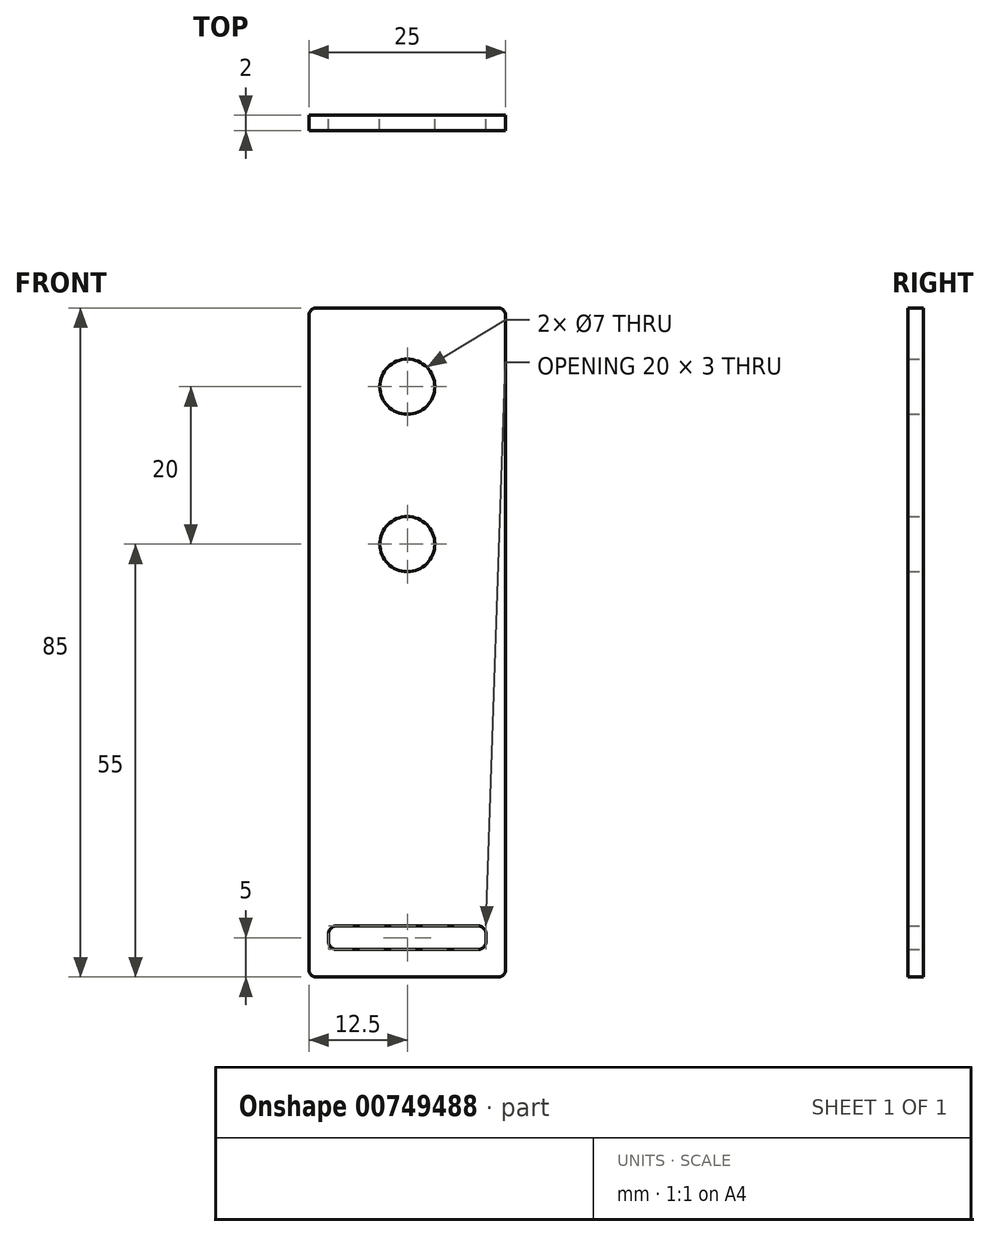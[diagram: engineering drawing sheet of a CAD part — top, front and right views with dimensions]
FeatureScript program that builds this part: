
annotation { "Feature Type Name" : "Feature", "Feature Type Description" : "" }
export const myFeature = defineFeature(function(context is Context, id is Id, definition is map)
    precondition{}
    {
        {
            var Q0;
            Q0=qCreatedBy(makeId("Front.planeOp"), FACE);
            var sketch = newSketch(context, id + "F0", { "sketchPlane" : qUnion([Q0])});
            skLineSegment(sketch, "E0.bottom", {"start": v(11.5, -42.5) * mm, "end": v(-11.5, -42.5) * mm});
            skLineSegment(sketch, "E0.top", {"start": v(11.5, 42.5) * mm, "end": v(-11.5, 42.5) * mm});
            skLineSegment(sketch, "E0.left", {"start": v(12.5, -41.5) * mm, "end": v(12.5, 41.5) * mm});
            skLineSegment(sketch, "E0.right", {"start": v(-12.5, -41.5) * mm, "end": v(-12.5, 41.5) * mm});
            skPoint(sketch, "E0.middle", {"position": v(0, 0) * mm});
            skLineSegment(sketch, "E1", {"start": v(0, 42.5) * mm, "end": v(0, -42.5) * mm, "construction": true});
            skLineSegment(sketch, "E2", {"start": v(-12.5, 32.5) * mm, "end": v(12.5, 32.5) * mm, "construction": true});
            skLineSegment(sketch, "E3", {"start": v(-12.5, 12.5) * mm, "end": v(12.5, 12.5) * mm, "construction": true});
            skLineSegment(sketch, "E4", {"start": v(-12.5, -37.5) * mm, "end": v(12.5, -37.5) * mm, "construction": true});
            skCircle(sketch, "E5", {"center": v(0, 32.5) * mm, "radius": 3.5 * mm});
            skCircle(sketch, "E6", {"center": v(0, 12.5) * mm, "radius": 3.5 * mm});
            skLineSegment(sketch, "E7.bottom", {"start": v(9, -39) * mm, "end": v(-9, -39) * mm});
            skLineSegment(sketch, "E7.top", {"start": v(9, -36) * mm, "end": v(-9, -36) * mm});
            skLineSegment(sketch, "E7.left", {"start": v(10, -38) * mm, "end": v(10, -37) * mm});
            skLineSegment(sketch, "E7.right", {"start": v(-10, -38) * mm, "end": v(-10, -37) * mm});
            skPoint(sketch, "E7.middle", {"position": v(0, -37.5) * mm});
            skPoint(sketch, "E8.visualSharp", {"position": v(10, -36) * mm});
            skArc(sketch, "E8.filletArc", {"start": v(10, -37) * mm, "mid": v(9.7, -36.3) * mm, "end": v(9, -36) * mm});
            skPoint(sketch, "E9.visualSharp", {"position": v(10, -39) * mm});
            skArc(sketch, "E9.filletArc", {"start": v(9, -39) * mm, "mid": v(9.7, -38.7) * mm, "end": v(10, -38) * mm});
            skPoint(sketch, "E10.visualSharp", {"position": v(-10, -39) * mm});
            skArc(sketch, "E10.filletArc", {"start": v(-10, -38) * mm, "mid": v(-9.7, -38.7) * mm, "end": v(-9, -39) * mm});
            skPoint(sketch, "E11.visualSharp", {"position": v(-10, -36) * mm});
            skArc(sketch, "E11.filletArc", {"start": v(-9, -36) * mm, "mid": v(-9.7, -36.3) * mm, "end": v(-10, -37) * mm});
            skPoint(sketch, "E12.visualSharp", {"position": v(-12.5, 42.5) * mm});
            skArc(sketch, "E12.filletArc", {"start": v(-11.5, 42.5) * mm, "mid": v(-12.2, 42.2) * mm, "end": v(-12.5, 41.5) * mm});
            skPoint(sketch, "E13.visualSharp", {"position": v(12.5, 42.5) * mm});
            skArc(sketch, "E13.filletArc", {"start": v(12.5, 41.5) * mm, "mid": v(12.2, 42.2) * mm, "end": v(11.5, 42.5) * mm});
            skPoint(sketch, "E14.visualSharp", {"position": v(12.5, -42.5) * mm});
            skArc(sketch, "E14.filletArc", {"start": v(11.5, -42.5) * mm, "mid": v(12.2, -42.2) * mm, "end": v(12.5, -41.5) * mm});
            skPoint(sketch, "E15.visualSharp", {"position": v(-12.5, -42.5) * mm});
            skArc(sketch, "E15.filletArc", {"start": v(-12.5, -41.5) * mm, "mid": v(-12.2, -42.2) * mm, "end": v(-11.5, -42.5) * mm});
            skSolve(sketch);
        }
        {
            var Q0;
            Q0 = qSketchRegion(id + "F0", true);
            extrude(context, id + "F1", {"entities" : qUnion([Q0]), "depth" : 2 * mm, "offsetDistance" : 25 * mm});
        }
    });
